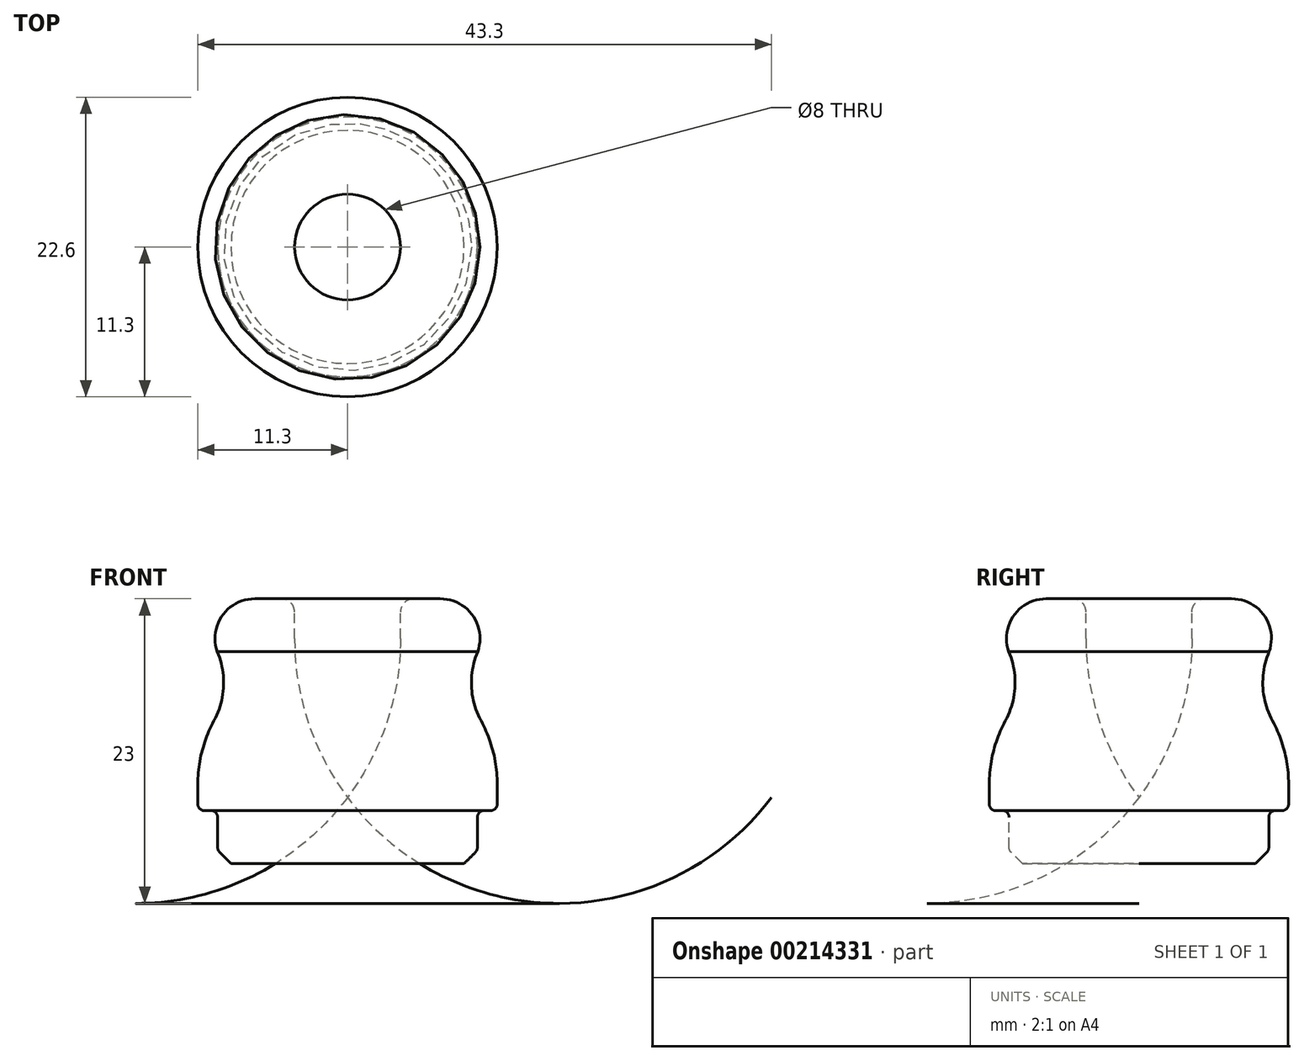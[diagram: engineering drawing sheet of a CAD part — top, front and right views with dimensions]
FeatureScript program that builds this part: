
annotation { "Feature Type Name" : "Feature", "Feature Type Description" : "" }
export const myFeature = defineFeature(function(context is Context, id is Id, definition is map)
    precondition{}
    {
        {
            var Q0;
            Q0=qCreatedBy(makeId("Front.planeOp"),FACE);
            var sketch = newSketch(context, id + "F0", { "sketchPlane" : qUnion([Q0])});
            skLineSegment(sketch, "E0", {"start": v(0, 0) * mm, "end": v(-9.8, 0) * mm});
            skLineSegment(sketch, "E1", {"start": v(-9.8, 0) * mm, "end": v(-9.8, 4) * mm});
            skLineSegment(sketch, "E2", {"start": v(-9.8, 4) * mm, "end": v(-11.3, 4) * mm});
            skLineSegment(sketch, "E3", {"start": v(-11.3, 4) * mm, "end": v(-11.3, 6) * mm});
            skLineSegment(sketch, "E4", {"start": v(0, 11.94) * mm, "end": v(0, -12.85) * mm, "construction": true});
            skArc(sketch, "E5", {"start": v(-11.3, 6) * mm, "mid": v(-11, 8.47) * mm, "end": v(-10.08, 10.78) * mm});
            skArc(sketch, "E6", {"start": v(-10.08, 10.78) * mm, "mid": v(-9.36, 13.36) * mm, "end": v(-9.83, 16) * mm});
            skLineSegment(sketch, "E7", {"start": v(-5, 20) * mm, "end": v(-7, 20) * mm});
            skArc(sketch, "E8", {"start": v(-7, 20) * mm, "mid": v(-9.45, 18.73) * mm, "end": v(-9.83, 16) * mm});
            skLineSegment(sketch, "E9", {"start": v(-4, 19) * mm, "end": v(-4, 17) * mm});
            skLineSegment(sketch, "E10", {"start": v(0, 5) * mm, "end": v(0, 0) * mm});
            skPoint(sketch, "E11.visualSharp", {"position": v(-4, 14.36) * mm});
            skPoint(sketch, "E12.visualSharp", {"position": v(-4, 20) * mm});
            skArc(sketch, "E12.filletArc", {"start": v(-4, 19) * mm, "mid": v(-4.3, 19.7) * mm, "end": v(-5, 20) * mm});
            skArc(sketch, "E13", {"start": v(-4, 17) * mm, "mid": v(-2.97, 10.68) * mm, "end": v(0, 5) * mm});
            skSolve(sketch);
        }
        {
            var Q0;
            Q0 = qSketchRegion(id + "F0", true);
            var Q1;
            Q1=sQuery(id+"F0.wireOp",EDGE,"E4");
            revolve(context, id + "F1", {"entities" : qUnion([Q0]), "axis" : qUnion([Q1]), "revolveType" : RevolveType.FULL});
        }
        {
            var Q0;
            Q0=makeQuery(id+"F1.opRevolve","SWEPT_EDGE",EDGE,{"disambiguationData":[OSD([sQuery(id+"F0.wireOp",EDGE,"E0"),sQuery(id+"F0.wireOp",EDGE,"E1")])]});
            chamfer(context, id + "F2", {"entities" : qUnion([Q0]), "width" : 1 * mm, "tangentPropagation" : true});
        }
        {
            var Q0;
            Q0=makeQuery(id+"F1.opRevolve","SWEPT_EDGE",EDGE,{"disambiguationData":[OSD([sQuery(id+"F0.wireOp",EDGE,"E1"),sQuery(id+"F0.wireOp",EDGE,"E2")])]});
            var Q1;
            Q1=makeQuery(id+"F1.opRevolve","SWEPT_EDGE",EDGE,{"disambiguationData":[OSD([sQuery(id+"F0.wireOp",EDGE,"E2"),sQuery(id+"F0.wireOp",EDGE,"E3")])]});
            var Q2;
            {var subQ0=sQuery(id+"F0.wireOp",EDGE,"E1");Q2=makeQuery(id+"F2.opChamfer","BLEND_EDGE",EDGE,{"blendedFrom":[makeQuery(id+"F1.opRevolve","SWEPT_EDGE",EDGE,{"disambiguationData":[OSD([sQuery(id+"F0.wireOp",EDGE,"E0"),subQ0])]}),makeQuery(id+"F1.opRevolve","SWEPT_FACE",FACE,{"disambiguationData":[OSD([subQ0])]})],"blendedInto":[makeQuery(id+"F1.opRevolve","SWEPT_FACE",FACE,{"disambiguationData":[OSD([subQ0])]})]});}
            fillet(context, id + "F3", {"entities" : qUnion([Q0, Q1, Q2]), "radius" : 0.5 * mm, "tangentPropagation" : true, "allowEdgeOverflow" : false});
        }
    });
